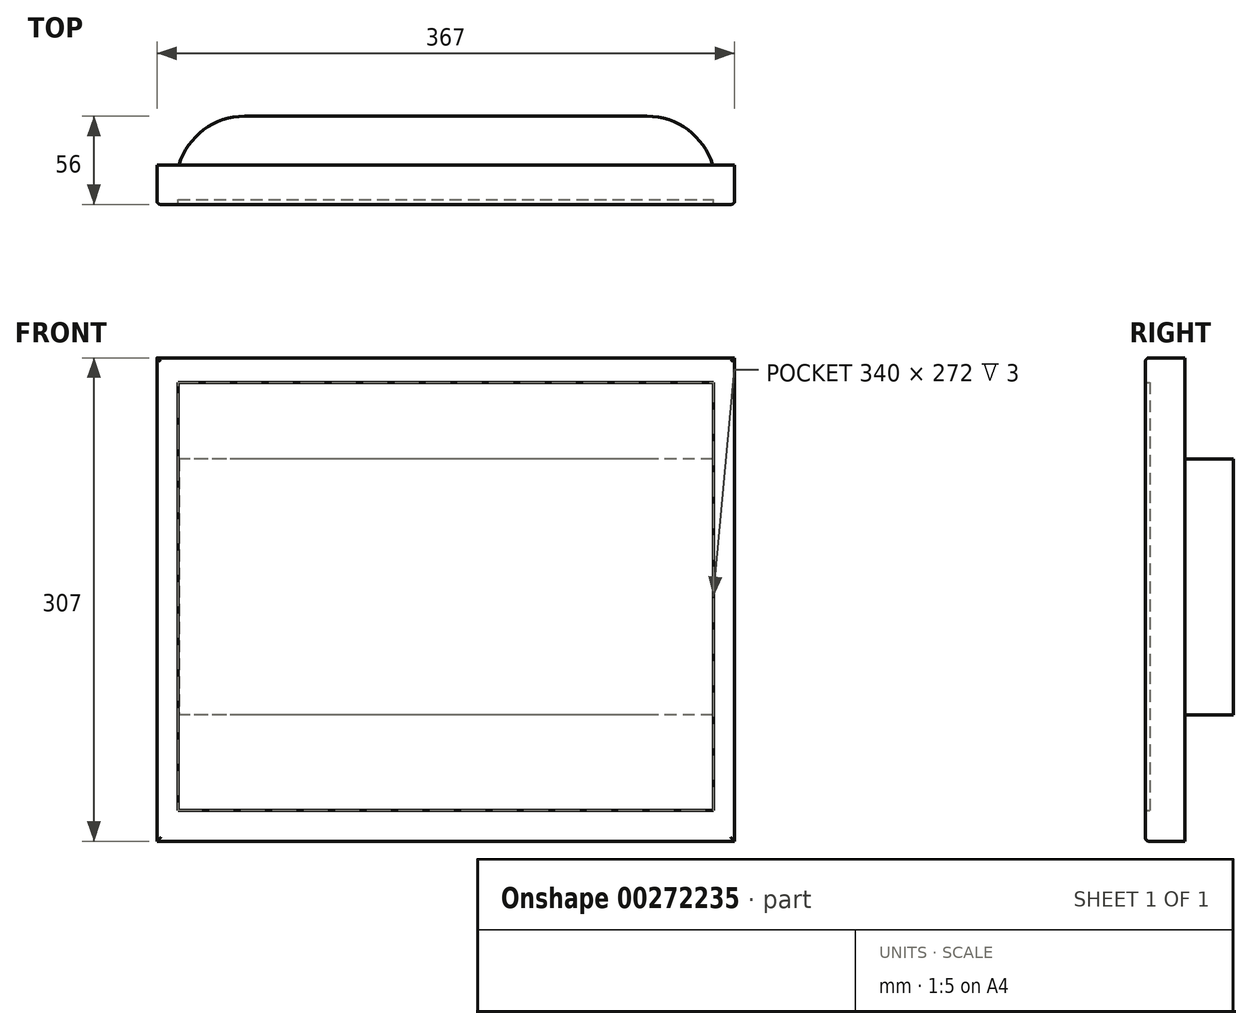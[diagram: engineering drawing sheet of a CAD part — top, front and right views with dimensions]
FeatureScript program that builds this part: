
annotation { "Feature Type Name" : "Feature", "Feature Type Description" : "" }
export const myFeature = defineFeature(function(context is Context, id is Id, definition is map)
    precondition{}
    {
        {
            var Q0;
            Q0=qCreatedBy(makeId("Front.planeOp"),FACE);
            var sketch = newSketch(context, id + "F0", { "sketchPlane" : qUnion([Q0])});
            skLineSegment(sketch, "E0.bottom", {"start": v(-183.5, -153.5) * mm, "end": v(183.5, -153.5) * mm});
            skLineSegment(sketch, "E0.top", {"start": v(-183.5, 153.5) * mm, "end": v(183.5, 153.5) * mm});
            skLineSegment(sketch, "E0.left", {"start": v(-183.5, -153.5) * mm, "end": v(-183.5, 153.5) * mm});
            skLineSegment(sketch, "E0.right", {"start": v(183.5, -153.5) * mm, "end": v(183.5, 153.5) * mm});
            skPoint(sketch, "E0.middle", {"position": v(0, 0) * mm});
            skLineSegment(sketch, "E1.bottom", {"start": v(-170, 138) * mm, "end": v(170, 138) * mm});
            skLineSegment(sketch, "E1.top", {"start": v(-170, -134) * mm, "end": v(170, -134) * mm});
            skLineSegment(sketch, "E1.left", {"start": v(-170, 138) * mm, "end": v(-170, -134) * mm});
            skLineSegment(sketch, "E1.right", {"start": v(170, 138) * mm, "end": v(170, -134) * mm});
            skSolve(sketch);
        }
        {
            var Q0;
            Q0=makeQuery(id+"F0.imprint","IMPRINT",FACE,{"disambiguationData":[TD([[makeQuery(id+"F0.imprint","IMPRINT",EDGE,{"derivedFrom":sQuery(id+"F0.wireOp",EDGE,"E0.bottom")}),1.0]])]});
            extrude(context, id + "F1", {"entities" : qUnion([Q0]), "depth" : 25 * mm});
        }
        {
            var Q0;
            Q0=makeQuery(id+"F0.imprint","IMPRINT",FACE,{"disambiguationData":[TD([[makeQuery(id+"F0.imprint","IMPRINT",EDGE,{"derivedFrom":sQuery(id+"F0.wireOp",EDGE,"E1.bottom")}),-1.0]])]});
            extrude(context, id + "F2", {"entities" : qUnion([Q0]), "operationType" : NewBodyOperationType.ADD, "depth" : 22 * mm});
        }
        {
            var Q0;
            Q0=makeQuery(id+"F1.opExtrude","CAP_EDGE",EDGE,{"disambiguationData":[OSD([sQuery(id+"F0.wireOp",EDGE,"E0.left")])],"isStart":false});
            var Q1;
            Q1=makeQuery(id+"F1.opExtrude","CAP_EDGE",EDGE,{"disambiguationData":[OSD([sQuery(id+"F0.wireOp",EDGE,"E0.right")])],"isStart":false});
            var Q2;
            Q2=makeQuery(id+"F1.opExtrude","CAP_EDGE",EDGE,{"disambiguationData":[OSD([sQuery(id+"F0.wireOp",EDGE,"E0.top")])],"isStart":false});
            var Q3;
            Q3=makeQuery(id+"F1.opExtrude","CAP_EDGE",EDGE,{"disambiguationData":[OSD([sQuery(id+"F0.wireOp",EDGE,"E0.bottom")])],"isStart":false});
            fillet(context, id + "F3", {"entities" : qUnion([Q0, Q1, Q2, Q3]), "radius" : 2.41 * mm, "tangentPropagation" : true, "allowEdgeOverflow" : false});
        }
        {
            var Q0;
            Q0=makeQuery(id+"F0.imprint","IMPRINT",FACE,{"disambiguationData":[TD([[makeQuery(id+"F0.imprint","IMPRINT",EDGE,{"derivedFrom":sQuery(id+"F0.wireOp",EDGE,"E0.bottom")}),1.0]])]});
            var sketch = newSketch(context, id + "F4", { "sketchPlane" : qUnion([Q0])});
            skLineSegment(sketch, "E2.bottom", {"start": v(169.5, 89.2) * mm, "end": v(-169.5, 89.2) * mm});
            skLineSegment(sketch, "E2.top", {"start": v(169.5, -73.3) * mm, "end": v(-169.5, -73.3) * mm});
            skLineSegment(sketch, "E2.left", {"start": v(169.5, 89.2) * mm, "end": v(169.5, -73.3) * mm});
            skLineSegment(sketch, "E2.right", {"start": v(-169.5, 89.2) * mm, "end": v(-169.5, -73.3) * mm});
            skSolve(sketch);
        }
        {
            var Q0;
            Q0 = qSketchRegion(id + "F4", true);
            extrude(context, id + "F5", {"entities" : qUnion([Q0]), "operationType" : NewBodyOperationType.ADD, "oppositeDirection" : true, "depth" : 31 * mm});
        }
        {
            var Q0;
            Q0=makeQuery(id+"F5.opExtrude","CAP_EDGE",EDGE,{"disambiguationData":[OSD([sQuery(id+"F4.wireOp",EDGE,"E2.left")])],"isStart":false});
            var Q1;
            Q1=makeQuery(id+"F5.opExtrude","CAP_EDGE",EDGE,{"disambiguationData":[OSD([sQuery(id+"F4.wireOp",EDGE,"E2.right")])],"isStart":false});
            fillet(context, id + "F6", {"entities" : qUnion([Q0, Q1]), "radius" : 43.46 * mm, "tangentPropagation" : true, "allowEdgeOverflow" : false});
        }
        {
            var Q0;
            Q0=makeQuery(id+"F1.opExtrude","CAP_FACE",FACE,{"disambiguationData":[OSD([sQuery(id+"F0.wireOp",EDGE,"E0.bottom"),sQuery(id+"F0.wireOp",EDGE,"E0.top"),sQuery(id+"F0.wireOp",EDGE,"E0.left"),sQuery(id+"F0.wireOp",EDGE,"E0.right"),sQuery(id+"F0.wireOp",EDGE,"E1.bottom"),sQuery(id+"F0.wireOp",EDGE,"E1.top"),sQuery(id+"F0.wireOp",EDGE,"E1.left"),sQuery(id+"F0.wireOp",EDGE,"E1.right")])],"isStart":false});
            var sketch = newSketch(context, id + "F7", { "sketchPlane" : qUnion([Q0])});
            skLineSegment(sketch, "E3.bottom", {"start": v(-170, 138) * mm, "end": v(170, 138) * mm});
            skLineSegment(sketch, "E3.top", {"start": v(-170, -134) * mm, "end": v(170, -134) * mm});
            skLineSegment(sketch, "E3.left", {"start": v(-170, 138) * mm, "end": v(-170, -134) * mm});
            skLineSegment(sketch, "E3.right", {"start": v(170, 138) * mm, "end": v(170, -134) * mm});
            skLineSegment(sketch, "E4.0", {"start": v(-172, 140) * mm, "end": v(172, 140) * mm});
            skLineSegment(sketch, "E4.1", {"start": v(-172, 140) * mm, "end": v(-172, -136) * mm});
            skLineSegment(sketch, "E4.2", {"start": v(-172, -136) * mm, "end": v(172, -136) * mm});
            skLineSegment(sketch, "E4.3", {"start": v(172, 140) * mm, "end": v(172, -136) * mm});
            skSolve(sketch);
        }
    });
